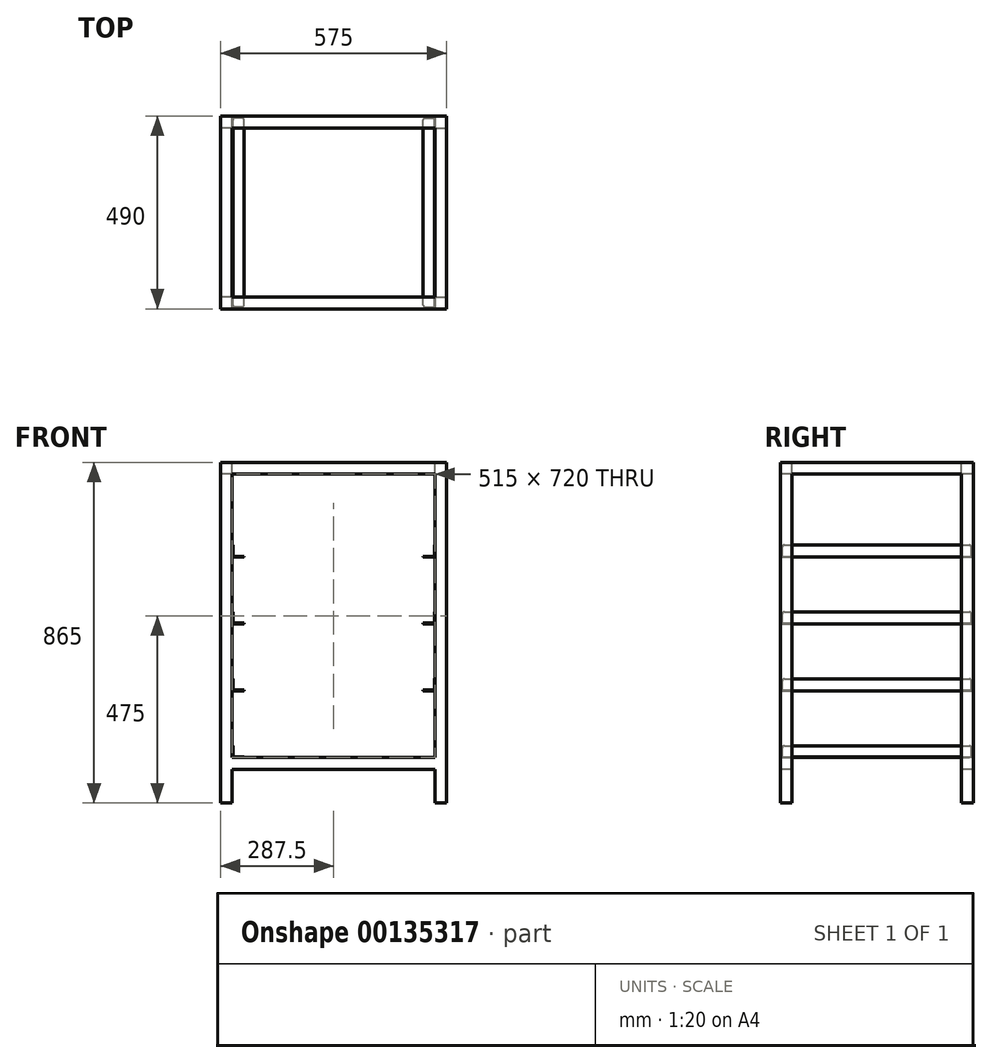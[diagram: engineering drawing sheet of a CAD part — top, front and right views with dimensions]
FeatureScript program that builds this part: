
annotation { "Feature Type Name" : "Feature", "Feature Type Description" : "" }
export const myFeature = defineFeature(function(context is Context, id is Id, definition is map)
    precondition{}
    {
        {
            var Q0;
            Q0=qCreatedBy(makeId("Top.planeOp"),FACE);
            var sketch = newSketch(context, id + "F0", { "sketchPlane" : qUnion([Q0])});
            skLineSegment(sketch, "E0.bottom", {"start": v(-287.5, -245) * mm, "end": v(-257.5, -245) * mm});
            skLineSegment(sketch, "E0.top", {"start": v(-287.5, -215) * mm, "end": v(-257.5, -215) * mm});
            skLineSegment(sketch, "E0.left", {"start": v(-287.5, -245) * mm, "end": v(-287.5, -215) * mm});
            skLineSegment(sketch, "E0.right", {"start": v(-257.5, -245) * mm, "end": v(-257.5, -215) * mm});
            skLineSegment(sketch, "E1.MirrorCS", {"start": v(287.5, -245) * mm, "end": v(257.5, -245) * mm});
            skLineSegment(sketch, "E2.MirrorCS", {"start": v(257.5, -245) * mm, "end": v(257.5, -215) * mm});
            skLineSegment(sketch, "E3.MirrorCS", {"start": v(287.5, -245) * mm, "end": v(287.5, -215) * mm});
            skLineSegment(sketch, "E4.MirrorCS", {"start": v(287.5, -215) * mm, "end": v(257.5, -215) * mm});
            skLineSegment(sketch, "E5.MirrorCS", {"start": v(-287.5, 245) * mm, "end": v(-257.5, 245) * mm});
            skLineSegment(sketch, "E6.MirrorCS", {"start": v(287.5, 215) * mm, "end": v(257.5, 215) * mm});
            skLineSegment(sketch, "E7.MirrorCS", {"start": v(287.5, 245) * mm, "end": v(287.5, 215) * mm});
            skLineSegment(sketch, "E8.MirrorCS", {"start": v(-287.5, 215) * mm, "end": v(-257.5, 215) * mm});
            skLineSegment(sketch, "E9.MirrorCS", {"start": v(-287.5, 245) * mm, "end": v(-287.5, 215) * mm});
            skLineSegment(sketch, "E10.MirrorCS", {"start": v(-257.5, 245) * mm, "end": v(-257.5, 215) * mm});
            skLineSegment(sketch, "E11.MirrorCS", {"start": v(287.5, 245) * mm, "end": v(257.5, 245) * mm});
            skLineSegment(sketch, "E12.MirrorCS", {"start": v(257.5, 245) * mm, "end": v(257.5, 215) * mm});
            skSolve(sketch);
        }
        {
            var Q0;
            Q0=makeQuery(id+"F0.imprint","IMPRINT",FACE,{"disambiguationData":[TD([[makeQuery(id+"F0.imprint","IMPRINT",EDGE,{"derivedFrom":sQuery(id+"F0.wireOp",EDGE,"E5.MirrorCS")}),-1.0]])]});
            var Q1;
            Q1=makeQuery(id+"F0.imprint","IMPRINT",FACE,{"disambiguationData":[TD([[makeQuery(id+"F0.imprint","IMPRINT",EDGE,{"derivedFrom":sQuery(id+"F0.wireOp",EDGE,"E6.MirrorCS")}),-1.0]])]});
            var Q2;
            Q2=makeQuery(id+"F0.imprint","IMPRINT",FACE,{"disambiguationData":[TD([[makeQuery(id+"F0.imprint","IMPRINT",EDGE,{"derivedFrom":sQuery(id+"F0.wireOp",EDGE,"E1.MirrorCS")}),-1.0]])]});
            var Q3;
            Q3=makeQuery(id+"F0.imprint","IMPRINT",FACE,{"disambiguationData":[TD([[makeQuery(id+"F0.imprint","IMPRINT",EDGE,{"derivedFrom":sQuery(id+"F0.wireOp",EDGE,"E0.bottom")}),1.0]])]});
            extrude(context, id + "F1", {"entities" : qUnion([Q0, Q1, Q2, Q3]), "offsetDistance" : 25 * mm, "depth" : 865 * mm});
        }
        {
            var Q0;
            Q0=qCreatedBy(makeId("Right.planeOp"),FACE);
            var sketch = newSketch(context, id + "F2", { "sketchPlane" : qUnion([Q0])});
            skLineSegment(sketch, "E13.bottom", {"start": v(-245, 115) * mm, "end": v(-215, 115) * mm});
            skLineSegment(sketch, "E13.top", {"start": v(-245, 85) * mm, "end": v(-215, 85) * mm});
            skLineSegment(sketch, "E13.left", {"start": v(-245, 115) * mm, "end": v(-245, 85) * mm});
            skLineSegment(sketch, "E13.right", {"start": v(-215, 115) * mm, "end": v(-215, 85) * mm});
            skLineSegment(sketch, "E14.MirrorCS", {"start": v(215, 115) * mm, "end": v(215, 85) * mm});
            skLineSegment(sketch, "E15.MirrorCS", {"start": v(245, 115) * mm, "end": v(245, 85) * mm});
            skLineSegment(sketch, "E16.MirrorCS", {"start": v(245, 85) * mm, "end": v(215, 85) * mm});
            skLineSegment(sketch, "E17.MirrorCS", {"start": v(245, 115) * mm, "end": v(215, 115) * mm});
            skLineSegment(sketch, "E18.bottom", {"start": v(-245, 865) * mm, "end": v(-215, 865) * mm});
            skLineSegment(sketch, "E18.top", {"start": v(-245, 835) * mm, "end": v(-215, 835) * mm});
            skLineSegment(sketch, "E18.left", {"start": v(-245, 865) * mm, "end": v(-245, 835) * mm});
            skLineSegment(sketch, "E18.right", {"start": v(-215, 865) * mm, "end": v(-215, 835) * mm});
            skLineSegment(sketch, "E19.MirrorCS", {"start": v(245, 865) * mm, "end": v(215, 865) * mm});
            skLineSegment(sketch, "E20.MirrorCS", {"start": v(245, 835) * mm, "end": v(215, 835) * mm});
            skLineSegment(sketch, "E21.MirrorCS", {"start": v(245, 865) * mm, "end": v(245, 835) * mm});
            skLineSegment(sketch, "E22.MirrorCS", {"start": v(215, 865) * mm, "end": v(215, 835) * mm});
            skSolve(sketch);
        }
        {
            var Q0;
            Q0 = qSketchRegion(id + "F2", true);
            extrude(context, id + "F3", {"entities" : qUnion([Q0]), "operationType" : NewBodyOperationType.ADD, "endBound" : BoundingType.UP_TO_NEXT, "depth" : 25 * mm, "hasSecondDirection" : true, "secondDirectionBound" : SecondDirectionBoundingType.UP_TO_NEXT, "secondDirectionOppositeDirection" : true, "secondDirectionDepth" : 25 * mm});
        }
        {
            var Q0;
            Q0=qCreatedBy(makeId("Front.planeOp"),FACE);
            var sketch = newSketch(context, id + "F4", { "sketchPlane" : qUnion([Q0])});
            skLineSegment(sketch, "E23.bottom", {"start": v(-287.5, 865) * mm, "end": v(-257.5, 865) * mm});
            skLineSegment(sketch, "E23.top", {"start": v(-287.5, 835) * mm, "end": v(-257.5, 835) * mm});
            skLineSegment(sketch, "E23.left", {"start": v(-287.5, 865) * mm, "end": v(-287.5, 835) * mm});
            skLineSegment(sketch, "E23.right", {"start": v(-257.5, 865) * mm, "end": v(-257.5, 835) * mm});
            skLineSegment(sketch, "E24.MirrorCS", {"start": v(287.5, 835) * mm, "end": v(257.5, 835) * mm});
            skLineSegment(sketch, "E25.MirrorCS", {"start": v(287.5, 865) * mm, "end": v(257.5, 865) * mm});
            skLineSegment(sketch, "E26.MirrorCS", {"start": v(287.5, 865) * mm, "end": v(287.5, 835) * mm});
            skLineSegment(sketch, "E27.MirrorCS", {"start": v(257.5, 865) * mm, "end": v(257.5, 835) * mm});
            skSolve(sketch);
        }
        {
            var Q0;
            Q0 = qSketchRegion(id + "F4", true);
            extrude(context, id + "F5", {"entities" : qUnion([Q0]), "operationType" : NewBodyOperationType.ADD, "endBound" : BoundingType.UP_TO_NEXT, "depth" : 25 * mm, "hasSecondDirection" : true, "secondDirectionBound" : SecondDirectionBoundingType.UP_TO_NEXT, "secondDirectionOppositeDirection" : true, "secondDirectionDepth" : 25 * mm});
        }
        {
            var Q0;
            Q0=makeQuery(id+"F3.boolean.opBoolean","SPLIT",FACE,{"disambiguationData":[TD([makeQuery(id+"F3.opExtrude","SWEPT_FACE",FACE,{"disambiguationData":[OSD([sQuery(id+"F2.wireOp",EDGE,"E13.bottom")])]})])],"derivedFrom":makeQuery(id+"F1.opExtrude","SWEPT_FACE",FACE,{"disambiguationData":[OSD([sQuery(id+"F0.wireOp",EDGE,"E0.right")])]})});
            var sketch = newSketch(context, id + "F6", { "sketchPlane" : qUnion([Q0])});
            skLineSegment(sketch, "E28.bottom", {"start": v(-240, 115) * mm, "end": v(240, 115) * mm});
            skLineSegment(sketch, "E28.top", {"start": v(-240, 145) * mm, "end": v(240, 145) * mm});
            skLineSegment(sketch, "E28.left", {"start": v(-240, 115) * mm, "end": v(-240, 145) * mm});
            skLineSegment(sketch, "E28.right", {"start": v(240, 115) * mm, "end": v(240, 145) * mm});
            skLineSegment(sketch, "E29.bottom", {"start": v(-240, 285) * mm, "end": v(240, 285) * mm});
            skLineSegment(sketch, "E29.top", {"start": v(-240, 315) * mm, "end": v(240, 315) * mm});
            skLineSegment(sketch, "E29.left", {"start": v(-240, 285) * mm, "end": v(-240, 315) * mm});
            skLineSegment(sketch, "E29.right", {"start": v(240, 285) * mm, "end": v(240, 315) * mm});
            skLineSegment(sketch, "E30.bottom", {"start": v(-240, 455) * mm, "end": v(240, 455) * mm});
            skLineSegment(sketch, "E30.top", {"start": v(-240, 485) * mm, "end": v(240, 485) * mm});
            skLineSegment(sketch, "E30.left", {"start": v(-240, 455) * mm, "end": v(-240, 485) * mm});
            skLineSegment(sketch, "E30.right", {"start": v(240, 455) * mm, "end": v(240, 485) * mm});
            skLineSegment(sketch, "E31.bottom", {"start": v(-240, 625) * mm, "end": v(240, 625) * mm});
            skLineSegment(sketch, "E31.top", {"start": v(-240, 655) * mm, "end": v(240, 655) * mm});
            skLineSegment(sketch, "E31.left", {"start": v(-240, 625) * mm, "end": v(-240, 655) * mm});
            skLineSegment(sketch, "E31.right", {"start": v(240, 625) * mm, "end": v(240, 655) * mm});
            skSolve(sketch);
        }
        {
            var Q0;
            Q0 = qSketchRegion(id + "F6", true);
            extrude(context, id + "F7", {"entities" : qUnion([Q0]), "depth" : 1.5 * mm});
        }
        {
            var Q0;
            Q0=makeQuery(id+"F7.opExtrude","CAP_FACE",FACE,{"disambiguationData":[OSD([sQuery(id+"F6.wireOp",EDGE,"E28.bottom"),sQuery(id+"F6.wireOp",EDGE,"E28.top"),sQuery(id+"F6.wireOp",EDGE,"E28.left"),sQuery(id+"F6.wireOp",EDGE,"E28.right")])],"isStart":false});
            var sketch = newSketch(context, id + "F8", { "sketchPlane" : qUnion([Q0])});
            skLineSegment(sketch, "E32.bottom", {"start": v(-240, 115) * mm, "end": v(240, 115) * mm});
            skLineSegment(sketch, "E32.top", {"start": v(-240, 116.5) * mm, "end": v(240, 116.5) * mm});
            skLineSegment(sketch, "E32.left", {"start": v(-240, 115) * mm, "end": v(-240, 116.5) * mm});
            skLineSegment(sketch, "E32.right", {"start": v(240, 115) * mm, "end": v(240, 116.5) * mm});
            skLineSegment(sketch, "E33.bottom", {"start": v(-240, 285) * mm, "end": v(240, 285) * mm});
            skLineSegment(sketch, "E33.top", {"start": v(-240, 286.5) * mm, "end": v(240, 286.5) * mm});
            skLineSegment(sketch, "E33.left", {"start": v(-240, 285) * mm, "end": v(-240, 286.5) * mm});
            skLineSegment(sketch, "E33.right", {"start": v(240, 285) * mm, "end": v(240, 286.5) * mm});
            skLineSegment(sketch, "E34.bottom", {"start": v(-240, 455) * mm, "end": v(240, 455) * mm});
            skLineSegment(sketch, "E34.top", {"start": v(-240, 456.5) * mm, "end": v(240, 456.5) * mm});
            skLineSegment(sketch, "E34.left", {"start": v(-240, 455) * mm, "end": v(-240, 456.5) * mm});
            skLineSegment(sketch, "E34.right", {"start": v(240, 455) * mm, "end": v(240, 456.5) * mm});
            skLineSegment(sketch, "E35.bottom", {"start": v(-240, 625) * mm, "end": v(240, 625) * mm});
            skLineSegment(sketch, "E35.top", {"start": v(-240, 626.5) * mm, "end": v(240, 626.5) * mm});
            skLineSegment(sketch, "E35.left", {"start": v(-240, 625) * mm, "end": v(-240, 626.5) * mm});
            skLineSegment(sketch, "E35.right", {"start": v(240, 625) * mm, "end": v(240, 626.5) * mm});
            skSolve(sketch);
        }
        {
            var Q0;
            Q0 = qSketchRegion(id + "F8", true);
            extrude(context, id + "F9", {"entities" : qUnion([Q0]), "operationType" : NewBodyOperationType.ADD, "depth" : (30 - 1.5) * mm});
        }
        {
            var Q0;
            Q0=makeQuery(id+"F7.opExtrude","SWEPT_EDGE",EDGE,{"disambiguationData":[OSD([sQuery(id+"F6.wireOp",EDGE,"E28.top"),sQuery(id+"F6.wireOp",EDGE,"E28.left")])]});
            var Q1;
            Q1=makeQuery(id+"F7.opExtrude","SWEPT_EDGE",EDGE,{"disambiguationData":[OSD([sQuery(id+"F6.wireOp",EDGE,"E28.top"),sQuery(id+"F6.wireOp",EDGE,"E28.right")])]});
            var Q2;
            Q2=makeQuery(id+"F9.opExtrude","CAP_EDGE",EDGE,{"disambiguationData":[OSD([sQuery(id+"F8.wireOp",EDGE,"E32.right")])],"isStart":false});
            var Q3;
            Q3=makeQuery(id+"F9.opExtrude","CAP_EDGE",EDGE,{"disambiguationData":[OSD([sQuery(id+"F8.wireOp",EDGE,"E32.left")])],"isStart":false});
            var Q4;
            Q4=makeQuery(id+"F7.opExtrude","SWEPT_EDGE",EDGE,{"disambiguationData":[OSD([sQuery(id+"F6.wireOp",EDGE,"E29.top"),sQuery(id+"F6.wireOp",EDGE,"E29.left")])]});
            var Q5;
            Q5=makeQuery(id+"F9.opExtrude","CAP_EDGE",EDGE,{"disambiguationData":[OSD([sQuery(id+"F8.wireOp",EDGE,"E33.left")])],"isStart":false});
            var Q6;
            Q6=makeQuery(id+"F9.opExtrude","CAP_EDGE",EDGE,{"disambiguationData":[OSD([sQuery(id+"F8.wireOp",EDGE,"E34.left")])],"isStart":false});
            var Q7;
            Q7=makeQuery(id+"F7.opExtrude","SWEPT_EDGE",EDGE,{"disambiguationData":[OSD([sQuery(id+"F6.wireOp",EDGE,"E30.top"),sQuery(id+"F6.wireOp",EDGE,"E30.left")])]});
            var Q8;
            Q8=makeQuery(id+"F9.opExtrude","CAP_EDGE",EDGE,{"disambiguationData":[OSD([sQuery(id+"F8.wireOp",EDGE,"E35.left")])],"isStart":false});
            var Q9;
            Q9=makeQuery(id+"F7.opExtrude","SWEPT_EDGE",EDGE,{"disambiguationData":[OSD([sQuery(id+"F6.wireOp",EDGE,"E31.top"),sQuery(id+"F6.wireOp",EDGE,"E31.left")])]});
            var Q10;
            Q10=makeQuery(id+"F7.opExtrude","SWEPT_EDGE",EDGE,{"disambiguationData":[OSD([sQuery(id+"F6.wireOp",EDGE,"E31.top"),sQuery(id+"F6.wireOp",EDGE,"E31.right")])]});
            var Q11;
            Q11=makeQuery(id+"F9.opExtrude","CAP_EDGE",EDGE,{"disambiguationData":[OSD([sQuery(id+"F8.wireOp",EDGE,"E35.right")])],"isStart":false});
            var Q12;
            Q12=makeQuery(id+"F9.opExtrude","CAP_EDGE",EDGE,{"disambiguationData":[OSD([sQuery(id+"F8.wireOp",EDGE,"E34.right")])],"isStart":false});
            var Q13;
            Q13=makeQuery(id+"F7.opExtrude","SWEPT_EDGE",EDGE,{"disambiguationData":[OSD([sQuery(id+"F6.wireOp",EDGE,"E30.top"),sQuery(id+"F6.wireOp",EDGE,"E30.right")])]});
            var Q14;
            Q14=makeQuery(id+"F9.opExtrude","CAP_EDGE",EDGE,{"disambiguationData":[OSD([sQuery(id+"F8.wireOp",EDGE,"E33.right")])],"isStart":false});
            var Q15;
            Q15=makeQuery(id+"F7.opExtrude","SWEPT_EDGE",EDGE,{"disambiguationData":[OSD([sQuery(id+"F6.wireOp",EDGE,"E29.top"),sQuery(id+"F6.wireOp",EDGE,"E29.right")])]});
            fillet(context, id + "F10", {"entities" : qUnion([Q0, Q1, Q2, Q3, Q4, Q5, Q6, Q7, Q8, Q9, Q10, Q11, Q12, Q13, Q14, Q15]), "radius" : 5 * mm, "tangentPropagation" : true, "allowEdgeOverflow" : false});
        }
        {
            var Q0;
            Q0=makeQuery(id+"F7.opExtrude","SWEPT_BODY",BODY,{"disambiguationData":[OSD([sQuery(id+"F6.wireOp",EDGE,"E31.bottom"),sQuery(id+"F6.wireOp",EDGE,"E31.top"),sQuery(id+"F6.wireOp",EDGE,"E31.left"),sQuery(id+"F6.wireOp",EDGE,"E31.right")])]});
            var Q1;
            Q1=makeQuery(id+"F7.opExtrude","SWEPT_BODY",BODY,{"disambiguationData":[OSD([sQuery(id+"F6.wireOp",EDGE,"E30.bottom"),sQuery(id+"F6.wireOp",EDGE,"E30.top"),sQuery(id+"F6.wireOp",EDGE,"E30.left"),sQuery(id+"F6.wireOp",EDGE,"E30.right")])]});
            var Q2;
            Q2=makeQuery(id+"F7.opExtrude","SWEPT_BODY",BODY,{"disambiguationData":[OSD([sQuery(id+"F6.wireOp",EDGE,"E29.bottom"),sQuery(id+"F6.wireOp",EDGE,"E29.top"),sQuery(id+"F6.wireOp",EDGE,"E29.left"),sQuery(id+"F6.wireOp",EDGE,"E29.right")])]});
            var Q3;
            Q3=makeQuery(id+"F7.opExtrude","SWEPT_BODY",BODY,{"disambiguationData":[OSD([sQuery(id+"F6.wireOp",EDGE,"E28.bottom"),sQuery(id+"F6.wireOp",EDGE,"E28.top"),sQuery(id+"F6.wireOp",EDGE,"E28.left"),sQuery(id+"F6.wireOp",EDGE,"E28.right")])]});
            var Q4;
            Q4=qCreatedBy(makeId("Right.planeOp"),FACE);
            mirror(context, id + "F11", {"operationType" : NewBodyOperationType.ADD, "entities" : qUnion([Q0, Q1, Q2, Q3]), "mirrorPlane" : qUnion([Q4])});
        }
    });
